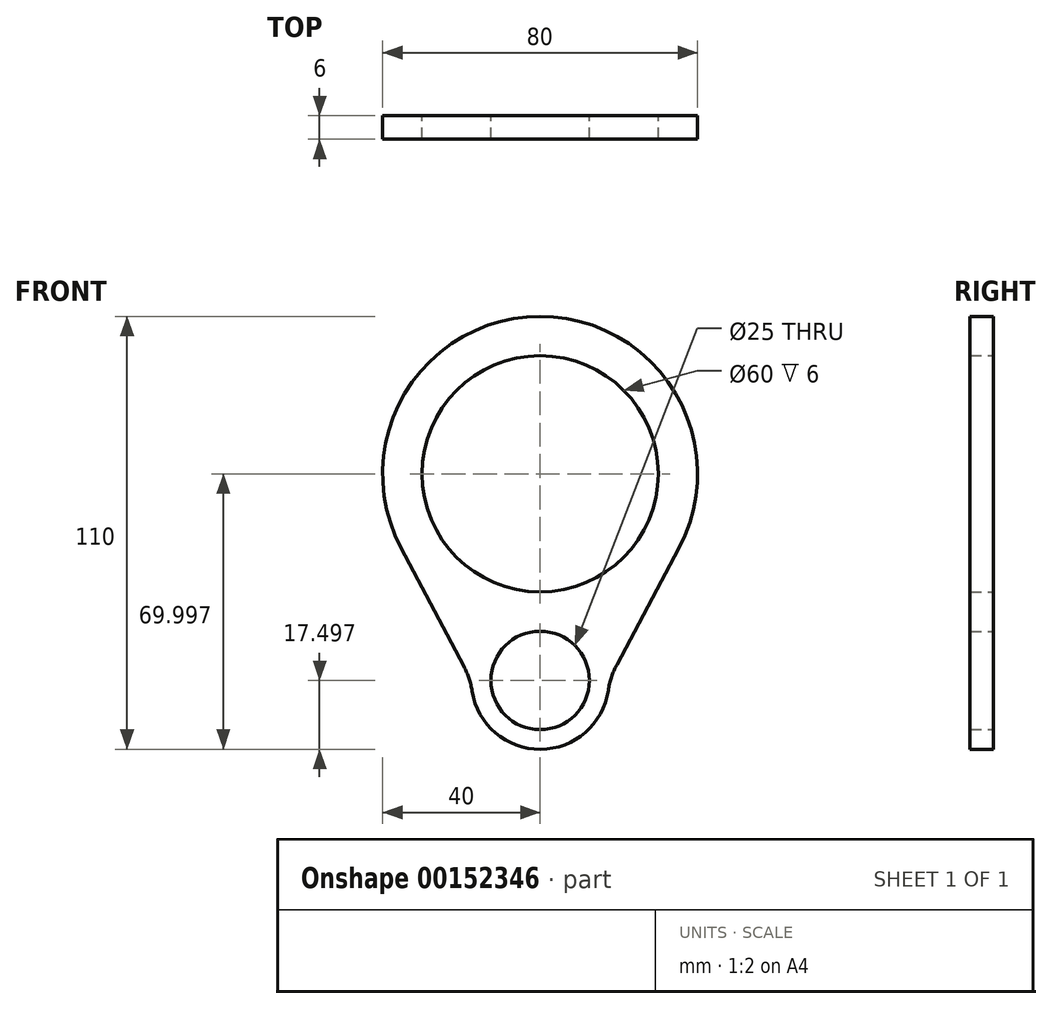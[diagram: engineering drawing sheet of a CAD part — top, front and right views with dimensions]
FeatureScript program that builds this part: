
annotation { "Feature Type Name" : "Feature", "Feature Type Description" : "" }
export const myFeature = defineFeature(function(context is Context, id is Id, definition is map)
    precondition{}
    {
        {
            var Q0;
            Q0=qCreatedBy(makeId("Front.planeOp"),FACE);
            var sketch = newSketch(context, id + "F0", { "sketchPlane" : qUnion([Q0])});
            skCircle(sketch, "E0", {"center": v(0, -33.68) * mm, "radius": 12.5 * mm});
            skCircle(sketch, "E1", {"center": v(0, 18.82) * mm, "radius": 30 * mm});
            skArc(sketch, "E2", {"start": v(35.3, 0) * mm, "mid": v(0, 58.82) * mm, "end": v(-35.3, 0) * mm});
            skArc(sketch, "E3", {"start": v(-17.5, -33.68) * mm, "mid": v(0.15, -51.18) * mm, "end": v(17.5, -33.4) * mm});
            skLineSegment(sketch, "E4", {"start": v(35.3, 0) * mm, "end": v(17.5, -33.4) * mm});
            skLineSegment(sketch, "E5", {"start": v(-35.3, 0) * mm, "end": v(-17.5, -33.68) * mm});
            skSolve(sketch);
        }
        {
            var Q0;
            Q0=makeQuery(id+"F0.imprint","IMPRINT",FACE,{"disambiguationData":[TD([[makeQuery(id+"F0.imprint","IMPRINT",EDGE,{"derivedFrom":sQuery(id+"F0.wireOp",EDGE,"E0")}),-1.0]])]});
            extrude(context, id + "F1", {"entities" : qUnion([Q0]), "depth" : 6 * mm});
        }
        {
            var Q0;
            Q0=makeQuery(id+"F1.opExtrude","SWEPT_EDGE",EDGE,{"disambiguationData":[OSD([sQuery(id+"F0.wireOp",EDGE,"E3"),sQuery(id+"F0.wireOp",EDGE,"E4")])]});
            var Q1;
            Q1=makeQuery(id+"F1.opExtrude","SWEPT_EDGE",EDGE,{"disambiguationData":[OSD([sQuery(id+"F0.wireOp",EDGE,"E3"),sQuery(id+"F0.wireOp",EDGE,"E5")])]});
            fillet(context, id + "F2", {"entities" : qUnion([Q0, Q1]), "radius" : 20 * mm, "tangentPropagation" : true, "allowEdgeOverflow" : false});
        }
    });
